# Revit family: IS_Idealrain_B9436_BIM_DE
name_source: partatom
category: Plumbing Fixtures
revit_build: Autodesk Revit 2015 (Build: 20140606_1530(x64)
units: mm (PartAtom-declared; Revit-internal decimal feet)

## types (1)
- B9436AA - Idealrain S1 Rainshower Fixed Shower Head With Angled Arm
    Assembly Code = C1030200
    AssetType = Fixed
    BIMObjectName = ISI_IdealStandard_ShowerMixers_CTV_A5784
    BarCode = 3800861024231
    Brand = Ideal Standard
    CWFU = 0
    Color = Chrome
    ConnectionType = Plumbing
    Cost = 0 $
    Default Elevation = 1219 mm
    Description = B9436AA IDEALRAIN rainshower head 100mm
    DurationUnit = year
    ExpectedLife = 25
    FaucetFunction = OTHER
    FaucetOperation = OTHER
    FaucetTopDescription = OTHER
    FaucetType = Mixer
    Features = IDEALRAIN rainshower head 100mm
    Finish = Chrome
    HWFU = 0
    InstallationDate = 0
    LinearUnits = millimeters
    ManufacturerURL = www.idealstandard.com
    Material = Varies
    Model = B9436AA
    ModelNumber = B9436AA
    ModelReference = B9436AA IDEALRAIN rainshower head 100mm
    NBSDescription = Shower mixers
    NBSReference = 45-35-70/335
    NettWeight = 0.5 Kg
    NominalHeight = 129 mm
    NominalLength = 171 mm
    NominalWidth = 100 mm  [stored 0.328084 ft]
    PredefinedType = Shower mixer
    ProductInformation = www.idealstandard.de/produkte
    Shape = Varies
    ShowerHeadDescription = Removable Handset
    ShowerType = Thermostatic
    Size = 171 x 129 x 100 mm
    Space = Internal
    TestPressure = 10 Bar
    URL = www.idealstandard.com
    Uniclass2015Code = Pr_40_20_87_81
    Uniclass2015Title = Shower thermostatic water supply sets
    Uniclass2015Version = Products v1.1
    Version = 1
    VolumeUnits = Litres
    WFU = 0
    WarrantyStartDate = 0
    WorkingPressure = 1-5 Bar

note: [stored X ft] marks values corroborated as IEEE doubles in the binary element streams (Revit-internal decimal feet)

## geometry (parser evidence)
native form markers: Blend x4, Sweep x1
no freeform markers — native parametric forms only
